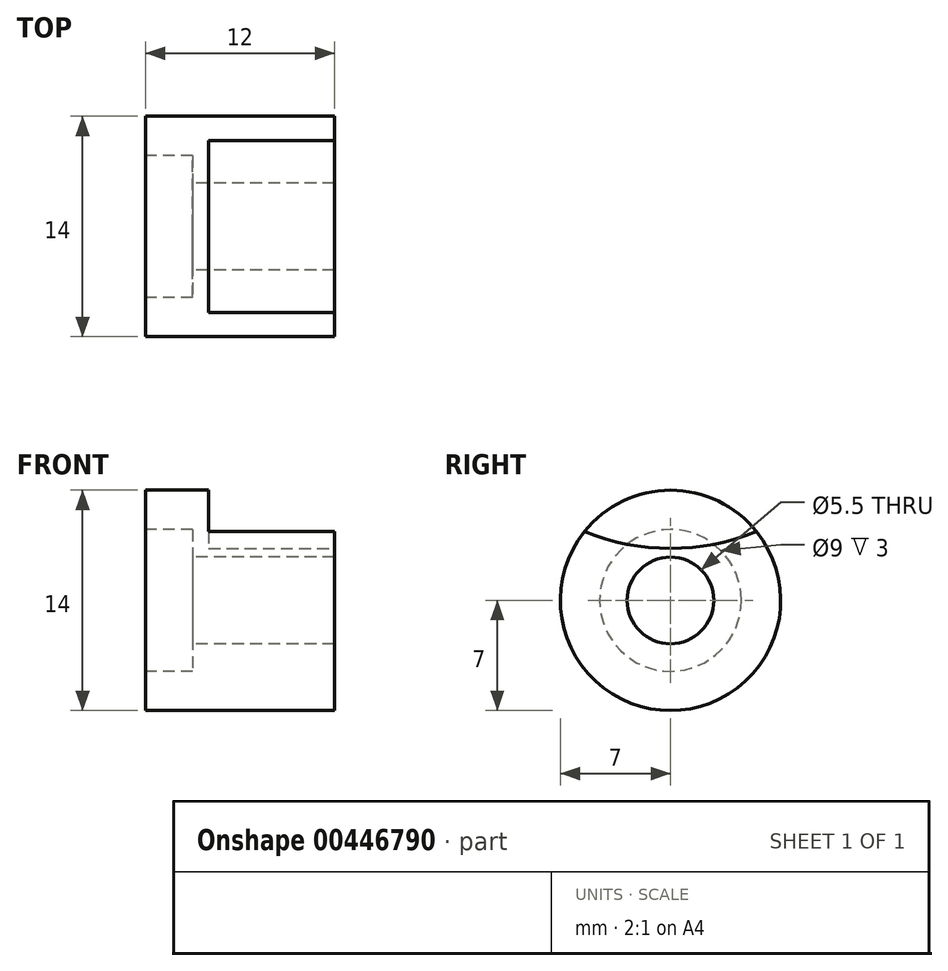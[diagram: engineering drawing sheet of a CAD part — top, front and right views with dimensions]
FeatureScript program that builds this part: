
annotation { "Feature Type Name" : "Feature", "Feature Type Description" : "" }
export const myFeature = defineFeature(function(context is Context, id is Id, definition is map)
    precondition{}
    {
        {
            var Q0;
            Q0=qCreatedBy(makeId("Right.planeOp"),FACE);
            var sketch = newSketch(context, id + "F0", { "sketchPlane" : qUnion([Q0])});
            skCircle(sketch, "E0", {"center": v(0, 0) * mm, "radius": 7 * mm});
            skSolve(sketch);
        }
        {
            var Q0;
            Q0 = qSketchRegion(id + "F0", true);
            extrude(context, id + "F1", {"entities" : qUnion([Q0]), "depth" : 12 * mm});
        }
        {
            var Q0;
            Q0=sQuery(id+"F0.wireOp",VERTEX,"E0.center");
            var Q1;
            Q1=makeQuery(id+"F1.opExtrude","SWEPT_BODY",BODY,{"disambiguationData":[OSD([sQuery(id+"F0.wireOp",EDGE,"E0")])]});
            hole(context, id + "F2", {"style" : HoleStyle.C_BORE, "endStyle" : HoleEndStyle.THROUGH, "oppositeDirection" : true, "holeDiameter" : 5.5 * mm, "cBoreDiameter" : 9 * mm, "cBoreDepth" : 3 * mm, "tappedDepth" : 12 * mm, "tapClearance" : 3, "startFromSketch" : true, "locations" : qUnion([Q0]), "scope" : qUnion([Q1])});
        }
        {
            var Q0;
            Q0=makeQuery(id+"F1.opExtrude","CAP_FACE",FACE,{"disambiguationData":[OSD([sQuery(id+"F0.wireOp",EDGE,"E0")])],"isStart":false});
            var sketch = newSketch(context, id + "F3", { "sketchPlane" : qUnion([Q0])});
            skArc(sketch, "E1", {"start": v(-5.47, 4.37) * mm, "mid": v(0, 3.3) * mm, "end": v(5.47, 4.37) * mm});
            skArc(sketch, "E2.0", {"start": v(5.47, 4.37) * mm, "mid": v(0, 7) * mm, "end": v(-5.47, 4.37) * mm});
            skSolve(sketch);
        }
        {
            var Q0;
            Q0 = qSketchRegion(id + "F3", true);
            extrude(context, id + "F4", {"entities" : qUnion([Q0]), "operationType" : NewBodyOperationType.REMOVE, "oppositeDirection" : true, "depth" : 8 * mm});
        }
    });
